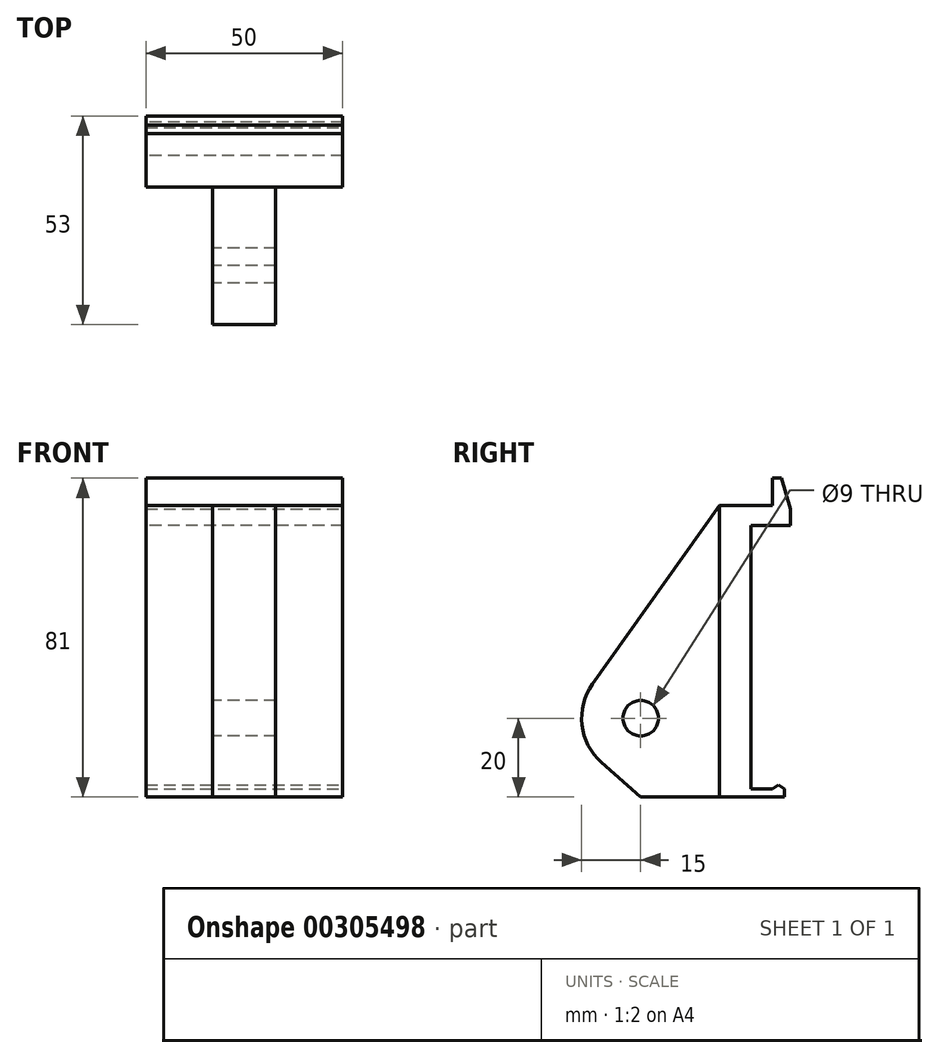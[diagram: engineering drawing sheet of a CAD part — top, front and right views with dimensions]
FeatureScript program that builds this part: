
annotation { "Feature Type Name" : "Feature", "Feature Type Description" : "" }
export const myFeature = defineFeature(function(context is Context, id is Id, definition is map)
    precondition{}
    {
        {
            var Q0;
            Q0=qCreatedBy(makeId("Right.planeOp"),FACE);
            var sketch = newSketch(context, id + "F0", { "sketchPlane" : qUnion([Q0])});
            skLineSegment(sketch, "E0", {"start": v(0, 0) * mm, "end": v(0, 7) * mm});
            skLineSegment(sketch, "E1", {"start": v(0, 7) * mm, "end": v(4.5, 7) * mm});
            skLineSegment(sketch, "E2", {"start": v(4.5, 7) * mm, "end": v(4.5, -5) * mm});
            skLineSegment(sketch, "E3", {"start": v(4.5, -5) * mm, "end": v(-5.5, -5) * mm});
            skLineSegment(sketch, "E4", {"start": v(-5.5, -5) * mm, "end": v(-5.5, -72) * mm});
            skLineSegment(sketch, "E5", {"start": v(-5.5, -72) * mm, "end": v(0, -72) * mm});
            skLineSegment(sketch, "E6", {"start": v(0, -72) * mm, "end": v(0, -71) * mm});
            skLineSegment(sketch, "E7", {"start": v(0, -71) * mm, "end": v(3, -71) * mm});
            skLineSegment(sketch, "E8", {"start": v(3, -71) * mm, "end": v(3, -74) * mm});
            skLineSegment(sketch, "E9", {"start": v(3, -74) * mm, "end": v(-13.5, -74) * mm});
            skLineSegment(sketch, "E10", {"start": v(0, 0) * mm, "end": v(-13.5, 0) * mm});
            skLineSegment(sketch, "E11", {"start": v(-13.5, -74) * mm, "end": v(-33.5, -74) * mm});
            skLineSegment(sketch, "E12", {"start": v(-33.5, -74) * mm, "end": v(-33.5, -54) * mm, "construction": true});
            skCircle(sketch, "E13", {"center": v(-33.5, -54) * mm, "radius": 4.5 * mm});
            skArc(sketch, "E14", {"start": v(-45.72, -45.3) * mm, "mid": v(-48.4, -55.72) * mm, "end": v(-43.42, -65.25) * mm});
            skLineSegment(sketch, "E15", {"start": v(-13.5, 0) * mm, "end": v(-45.72, -45.3) * mm});
            skLineSegment(sketch, "E16", {"start": v(-33.5, -74) * mm, "end": v(-43.42, -65.25) * mm});
            skSolve(sketch);
        }
        {
            var Q0;
            Q0=makeQuery(id+"F0.imprint","IMPRINT",FACE,{"disambiguationData":[TD([[makeQuery(id+"F0.imprint","IMPRINT",EDGE,{"derivedFrom":sQuery(id+"F0.wireOp",EDGE,"E0")}),-1.0]])]});
            extrude(context, id + "F1", {"entities" : qUnion([Q0]), "endBound" : BoundingType.SYMMETRIC, "depth" : 50 * mm});
        }
        {
            var Q0;
            Q0=makeQuery(id+"F1.opExtrude","CAP_FACE",FACE,{"disambiguationData":[OSD([sQuery(id+"F0.wireOp",EDGE,"E0"),sQuery(id+"F0.wireOp",EDGE,"E1"),sQuery(id+"F0.wireOp",EDGE,"E2"),sQuery(id+"F0.wireOp",EDGE,"E3"),sQuery(id+"F0.wireOp",EDGE,"E4"),sQuery(id+"F0.wireOp",EDGE,"E5"),sQuery(id+"F0.wireOp",EDGE,"E6"),sQuery(id+"F0.wireOp",EDGE,"E7"),sQuery(id+"F0.wireOp",EDGE,"E8"),sQuery(id+"F0.wireOp",EDGE,"E9"),sQuery(id+"F0.wireOp",EDGE,"E10"),sQuery(id+"F0.wireOp",EDGE,"E11"),sQuery(id+"F0.wireOp",EDGE,"E13"),sQuery(id+"F0.wireOp",EDGE,"E14"),sQuery(id+"F0.wireOp",EDGE,"E15"),sQuery(id+"F0.wireOp",EDGE,"E16")])],"isStart":false});
            var sketch = newSketch(context, id + "F2", { "sketchPlane" : qUnion([Q0])});
            skLineSegment(sketch, "E17", {"start": v(0, 7) * mm, "end": v(2.2, 7) * mm, "construction": true});
            skLineSegment(sketch, "E18", {"start": v(2.2, 7) * mm, "end": v(4.5, -0.82) * mm});
            skLineSegment(sketch, "E19", {"start": v(4.5, -0.82) * mm, "end": v(4.5, 7) * mm});
            skLineSegment(sketch, "E20", {"start": v(4.5, 7) * mm, "end": v(2.2, 7) * mm});
            skSolve(sketch);
        }
        {
            var Q0;
            Q0=makeQuery(id+"F2.imprint","IMPRINT",FACE,{"disambiguationData":[TD([[makeQuery(id+"F2.imprint","IMPRINT",EDGE,{"derivedFrom":sQuery(id+"F2.wireOp",EDGE,"E18")}),1.0]])]});
            extrude(context, id + "F3", {"entities" : qUnion([Q0]), "operationType" : NewBodyOperationType.REMOVE, "endBound" : BoundingType.UP_TO_NEXT, "oppositeDirection" : true, "depth" : 25 * mm});
        }
        {
            var Q0;
            Q0=makeQuery(id+"F1.opExtrude","CAP_FACE",FACE,{"disambiguationData":[OSD([sQuery(id+"F0.wireOp",EDGE,"E0"),sQuery(id+"F0.wireOp",EDGE,"E1"),sQuery(id+"F0.wireOp",EDGE,"E2"),sQuery(id+"F0.wireOp",EDGE,"E3"),sQuery(id+"F0.wireOp",EDGE,"E4"),sQuery(id+"F0.wireOp",EDGE,"E5"),sQuery(id+"F0.wireOp",EDGE,"E6"),sQuery(id+"F0.wireOp",EDGE,"E7"),sQuery(id+"F0.wireOp",EDGE,"E8"),sQuery(id+"F0.wireOp",EDGE,"E9"),sQuery(id+"F0.wireOp",EDGE,"E10"),sQuery(id+"F0.wireOp",EDGE,"E11"),sQuery(id+"F0.wireOp",EDGE,"E13"),sQuery(id+"F0.wireOp",EDGE,"E14"),sQuery(id+"F0.wireOp",EDGE,"E15"),sQuery(id+"F0.wireOp",EDGE,"E16")])],"isStart":false});
            var sketch = newSketch(context, id + "F4", { "sketchPlane" : qUnion([Q0])});
            skLineSegment(sketch, "E21", {"start": v(0, -72) * mm, "end": v(1.5, -71) * mm});
            skLineSegment(sketch, "E22", {"start": v(1.5, -71) * mm, "end": v(3, -72) * mm});
            skPoint(sketch, "E22.endSnap0", {"position": v(3, -72.5) * mm});
            skLineSegment(sketch, "E23", {"start": v(0, -72) * mm, "end": v(0, -71) * mm});
            skLineSegment(sketch, "E24", {"start": v(0, -71) * mm, "end": v(1.5, -71) * mm});
            skLineSegment(sketch, "E25", {"start": v(3, -71) * mm, "end": v(3, -72) * mm});
            skSolve(sketch);
        }
        {
            var Q0;
            Q0=makeQuery(id+"F4.imprint","IMPRINT",FACE,{"disambiguationData":[TD([[makeQuery(id+"F4.imprint","IMPRINT",EDGE,{"derivedFrom":sQuery(id+"F4.wireOp",EDGE,"E21")}),1.0]])]});
            var Q1;
            {var subQ0=sQuery(id+"F4.wireOp",EDGE,"E22");Q1=makeQuery(id+"F4.imprint","IMPRINT",FACE,{"disambiguationData":[TD([[makeQuery(id+"F4.imprint","IMPRINT",EDGE,{"derivedFrom":subQ0}),1.0]])]});}
            extrude(context, id + "F5", {"entities" : qUnion([Q0, Q1]), "operationType" : NewBodyOperationType.REMOVE, "endBound" : BoundingType.UP_TO_NEXT, "oppositeDirection" : true, "depth" : 25 * mm});
        }
        {
            var Q0;
            Q0=makeQuery(id+"F1.opExtrude","CAP_FACE",FACE,{"disambiguationData":[OSD([sQuery(id+"F0.wireOp",EDGE,"E0"),sQuery(id+"F0.wireOp",EDGE,"E1"),sQuery(id+"F0.wireOp",EDGE,"E2"),sQuery(id+"F0.wireOp",EDGE,"E3"),sQuery(id+"F0.wireOp",EDGE,"E4"),sQuery(id+"F0.wireOp",EDGE,"E5"),sQuery(id+"F0.wireOp",EDGE,"E6"),sQuery(id+"F0.wireOp",EDGE,"E7"),sQuery(id+"F0.wireOp",EDGE,"E8"),sQuery(id+"F0.wireOp",EDGE,"E9"),sQuery(id+"F0.wireOp",EDGE,"E10"),sQuery(id+"F0.wireOp",EDGE,"E11"),sQuery(id+"F0.wireOp",EDGE,"E13"),sQuery(id+"F0.wireOp",EDGE,"E14"),sQuery(id+"F0.wireOp",EDGE,"E15"),sQuery(id+"F0.wireOp",EDGE,"E16")])],"isStart":false});
            var sketch = newSketch(context, id + "F6", { "sketchPlane" : qUnion([Q0])});
            skLineSegment(sketch, "E26", {"start": v(-13.5, 0) * mm, "end": v(-13.5, -74) * mm});
            skLineSegment(sketch, "E27", {"start": v(-13.5, -74) * mm, "end": v(-59.7, -74) * mm});
            skLineSegment(sketch, "E28", {"start": v(-59.7, -74) * mm, "end": v(-59.7, 0) * mm});
            skLineSegment(sketch, "E29", {"start": v(-59.7, 0) * mm, "end": v(-13.5, 0) * mm});
            skSolve(sketch);
        }
        {
            var Q0;
            {var subQ2=sQuery(id+"F6.wireOp",EDGE,"E26");Q0=makeQuery(id+"F6.imprint","IMPRINT",FACE,{"disambiguationData":[TD([[makeQuery(id+"F6.imprint","IMPRINT",EDGE,{"derivedFrom":subQ2}),-1.0]])]});}
            extrude(context, id + "F7", {"entities" : qUnion([Q0]), "operationType" : NewBodyOperationType.REMOVE, "oppositeDirection" : true, "depth" : 17 * mm});
        }
        {
            var Q0;
            Q0=makeQuery(id+"F1.opExtrude","CAP_FACE",FACE,{"disambiguationData":[OSD([sQuery(id+"F0.wireOp",EDGE,"E0"),sQuery(id+"F0.wireOp",EDGE,"E1"),sQuery(id+"F0.wireOp",EDGE,"E2"),sQuery(id+"F0.wireOp",EDGE,"E3"),sQuery(id+"F0.wireOp",EDGE,"E4"),sQuery(id+"F0.wireOp",EDGE,"E5"),sQuery(id+"F0.wireOp",EDGE,"E6"),sQuery(id+"F0.wireOp",EDGE,"E7"),sQuery(id+"F0.wireOp",EDGE,"E8"),sQuery(id+"F0.wireOp",EDGE,"E9"),sQuery(id+"F0.wireOp",EDGE,"E10"),sQuery(id+"F0.wireOp",EDGE,"E11"),sQuery(id+"F0.wireOp",EDGE,"E13"),sQuery(id+"F0.wireOp",EDGE,"E14"),sQuery(id+"F0.wireOp",EDGE,"E15"),sQuery(id+"F0.wireOp",EDGE,"E16")])],"isStart":true});
            var sketch = newSketch(context, id + "F8", { "sketchPlane" : qUnion([Q0])});
            skLineSegment(sketch, "E30", {"start": v(13.5, 0) * mm, "end": v(13.5, -74) * mm});
            skLineSegment(sketch, "E31", {"start": v(13.5, -74) * mm, "end": v(50.7, -74) * mm});
            skPoint(sketch, "E31.endSnap0", {"position": v(15.25, -74) * mm});
            skLineSegment(sketch, "E32", {"start": v(50.7, -74) * mm, "end": v(50.7, 0) * mm});
            skLineSegment(sketch, "E33", {"start": v(50.7, 0) * mm, "end": v(13.5, 0) * mm});
            skSolve(sketch);
        }
        {
            var Q0;
            {var subQ2=sQuery(id+"F8.wireOp",EDGE,"E30");Q0=makeQuery(id+"F8.imprint","IMPRINT",FACE,{"disambiguationData":[TD([[makeQuery(id+"F8.imprint","IMPRINT",EDGE,{"derivedFrom":subQ2}),1.0]])]});}
            extrude(context, id + "F9", {"entities" : qUnion([Q0]), "operationType" : NewBodyOperationType.REMOVE, "oppositeDirection" : true, "depth" : 17 * mm});
        }
    });
